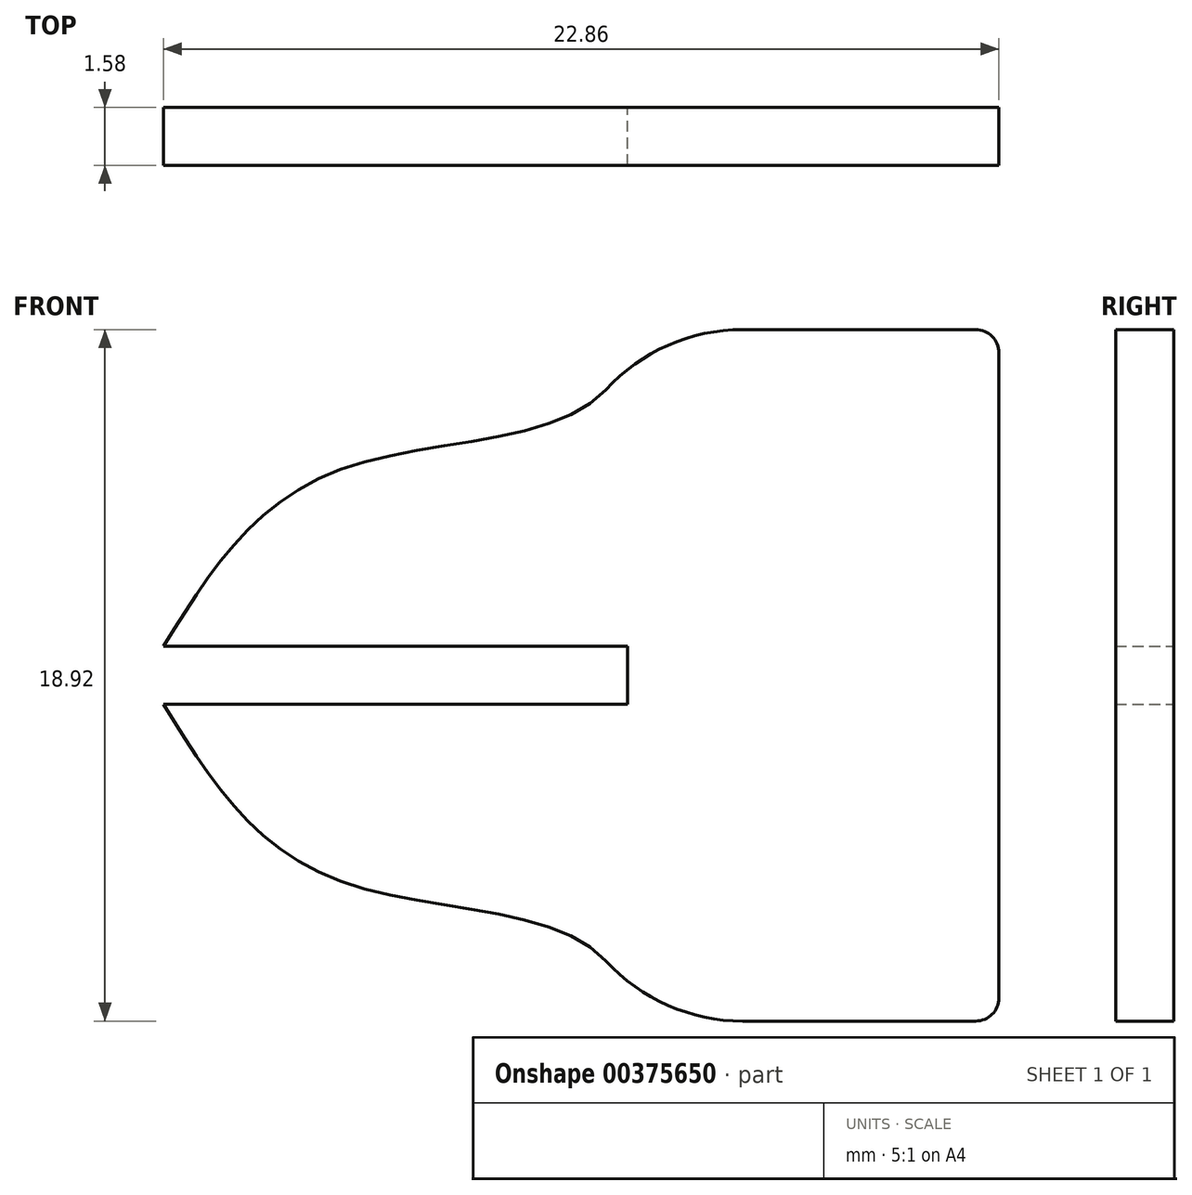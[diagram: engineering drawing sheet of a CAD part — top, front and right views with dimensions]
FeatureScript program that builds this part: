
annotation { "Feature Type Name" : "Feature", "Feature Type Description" : "" }
export const myFeature = defineFeature(function(context is Context, id is Id, definition is map)
    precondition{}
    {
        {
            var Q0;
            Q0=qCreatedBy(makeId("Front.planeOp"),FACE);
            var sketch = newSketch(context, id + "F0", { "sketchPlane" : qUnion([Q0])});
            skLineSegment(sketch, "E0", {"start": v(-22.9, 0) * mm, "end": v(14.27, 0) * mm, "construction": true});
            skLineSegment(sketch, "E1.bottom", {"start": v(5.08, -9.46) * mm, "end": v(-5.08, -9.46) * mm});
            skLineSegment(sketch, "E1.top", {"start": v(5.08, 9.46) * mm, "end": v(-5.08, 9.46) * mm});
            skLineSegment(sketch, "E1.left", {"start": v(5.08, -9.46) * mm, "end": v(5.08, 9.46) * mm});
            skPoint(sketch, "E1.middle", {"position": v(0, 0) * mm});
            skLineSegment(sketch, "E2", {"start": v(-17.78, 0.8) * mm, "end": v(-5.08, 0.8) * mm});
            skLineSegment(sketch, "E3", {"start": v(-5.08, 0.8) * mm, "end": v(-5.08, -0.8) * mm});
            skLineSegment(sketch, "E4", {"start": v(-5.08, -0.8) * mm, "end": v(-17.78, -0.8) * mm});
            skPoint(sketch, "E5.MirrorCS.start.orphan", {"position": v(-5.08, -9.46) * mm});
            skFitSpline(sketch, "E6", {"points": [v(-5.08, 9.46) * mm, v(-12.7, 5.72) * mm, v(-17.78, 0.8) * mm], "startDerivative": vector(0, -18.8) * mm, "endDerivative": vector(-7.64, -12.16) * mm});
            skFitSpline(sketch, "E7.MirrorCS", {"points": [v(-5.08, -9.46) * mm, v(-12.7, -5.72) * mm, v(-17.78, -0.8) * mm], "startDerivative": vector(0, 18.8) * mm, "endDerivative": vector(-7.64, 12.16) * mm});
            skSolve(sketch);
        }
        {
            var Q0;
            Q0=qSketchRegion(id+"F0",true);
            extrude(context, id + "F1", {"entities" : qUnion([Q0]), "endBound" : BoundingType.SYMMETRIC, "depth" : 1.59 * mm});
        }
        {
            var Q0;
            Q0=makeQuery(id+"F1.opExtrude","SWEPT_EDGE",EDGE,{"disambiguationData":[OSD([sQuery(id+"F0.wireOp",EDGE,"E1.top"),sQuery(id+"F0.wireOp",EDGE,"E1.left")])]});
            var Q1;
            Q1=makeQuery(id+"F1.opExtrude","SWEPT_EDGE",EDGE,{"disambiguationData":[OSD([sQuery(id+"F0.wireOp",EDGE,"E1.bottom"),sQuery(id+"F0.wireOp",EDGE,"E1.left")])]});
            fillet(context, id + "F2", {"entities" : qUnion([Q0, Q1]), "radius" : 0.64 * mm, "tangentPropagation" : true, "allowEdgeOverflow" : false});
        }
        {
            var Q0;
            Q0=makeQuery(id+"F1.opExtrude","SWEPT_EDGE",EDGE,{"disambiguationData":[OSD([sQuery(id+"F0.wireOp",EDGE,"E1.top"),sQuery(id+"F0.wireOp",EDGE,"E6")])]});
            var Q1;
            Q1=makeQuery(id+"F1.opExtrude","SWEPT_EDGE",EDGE,{"disambiguationData":[OSD([sQuery(id+"F0.wireOp",EDGE,"E1.bottom"),sQuery(id+"F0.wireOp",EDGE,"E7.MirrorCS")])]});
            fillet(context, id + "F3", {"entities" : qUnion([Q0, Q1]), "radius" : 5.08 * mm, "tangentPropagation" : true, "allowEdgeOverflow" : false});
        }
    });
